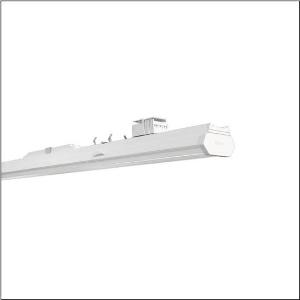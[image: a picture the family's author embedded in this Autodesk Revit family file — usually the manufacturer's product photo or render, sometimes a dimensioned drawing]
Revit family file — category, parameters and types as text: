
# Revit family: licross_r__21_protected_mo_52td12dn4a5g3c_a968
name_source: partatom
category: Lighting Fixtures
units: mm (PartAtom-declared; Revit-internal decimal feet)

## family parameters
Cut with Voids When Loaded = No
Host = Face
Light Source = No
Part Type = Normal
Room Calculation Point = No
Round Connector Dimension = Use Diameter
Shared = No

## types (1)
- --- (1 x LED, 940 lm, 6.8 W, 4000K)
    Apparent Load = 7 VA
    CIE Flux Codes = 73 92 98 99 100
    Color Rendering = 80
    Color Temperature = 4000K
    Default Elevation = 1800 mm
    Description = Licross® 21 Protected MO, luminaire insert, of sheet steel, galvanised, coil coated, white, length: 1.500mm, width: 90mm, height: 103mm, LED rated luminous flux: 10.700lm, light colour: 840, control gear: DALI 2, with plug, 6-pole, with phase selection, for trunking rail, 14-core, mains connection: 220..240V, AC, 50/60Hz, rated input power: 66W, for trunking rail, 14-core, halogen-free wiring, for emergency light function, converter,control gear: single battery element, battery: LiFeP04, 9Ah, primary light control with lens, of plastic, primary optical cover: cover, of PMMA, light emission: direct distribution, primary light characteristic: symmetric, protection rating (complete): IP54, insulation class (complete): insulation class I (protective earthing), certification: CE, UKCA, protection symbol: D if used in an environment with non-conductive dust loads with corresponding accessories, impact resistance: IK06, permissible ambient temperature for indoor applications: +5..+35°C, standard: EN 60598-2-22, LABS conformity tested according to VDMA 24364:2018-05, reducing of maximum allowable ambient temperature of 5°C with ceiling mounting, corresponds to IFS (International Featured Standards) requirements for safety and quality in the food industry, packaging unit: 1 piece
    Height = 92 mm
    Lamp = 1 x LED
    Lamp Light Flux = 940 lm
    Lamp Power = 6.8 W
    Lamp count = 1
    Length = 1500 mm
    Luminous efficacy = 138 lm/W
    Manufacturer = Siteco
    ModVariant = No
    Model = 52TD12DN4A5G3C
    Mounting Place = Ceiling
    Mounting Type = Pendant
    Number of Poles = 1
    OnlyDefault = Yes
    Power Factor = 1
    Product Name = Licross® 21 Protected MO
    Product group = luminaire insert
    ProductGroupID = 901
    Protection Class = Protection class I
    Protection Degree = IP 54
    RLX_Detail_Level = 1
    RLX_Emergency_Light_Flux = 0 lm
    RLX_Emergency_Type = 0
    RLX_Emergency_Type_DB = No
    RlxData = <blob elided: 24853 chars, md5=26a8a9f4>
    Socket = socket
    Standby Power = 0 W
    System Light Flux = 940 lm
    System Power = 7 W
    Type Comments = : emergency light operation: 3 h
    Type Image = l_1256148.jpg
    URL = http://relux.com
    VarID = @adj_041015
    Voltage = 0 V
    Weight = 0.00 kg
    Width = 88 mm

## geometry (parser evidence)
native form markers: Blend x4, Sweep x11
no freeform markers — native parametric forms only
